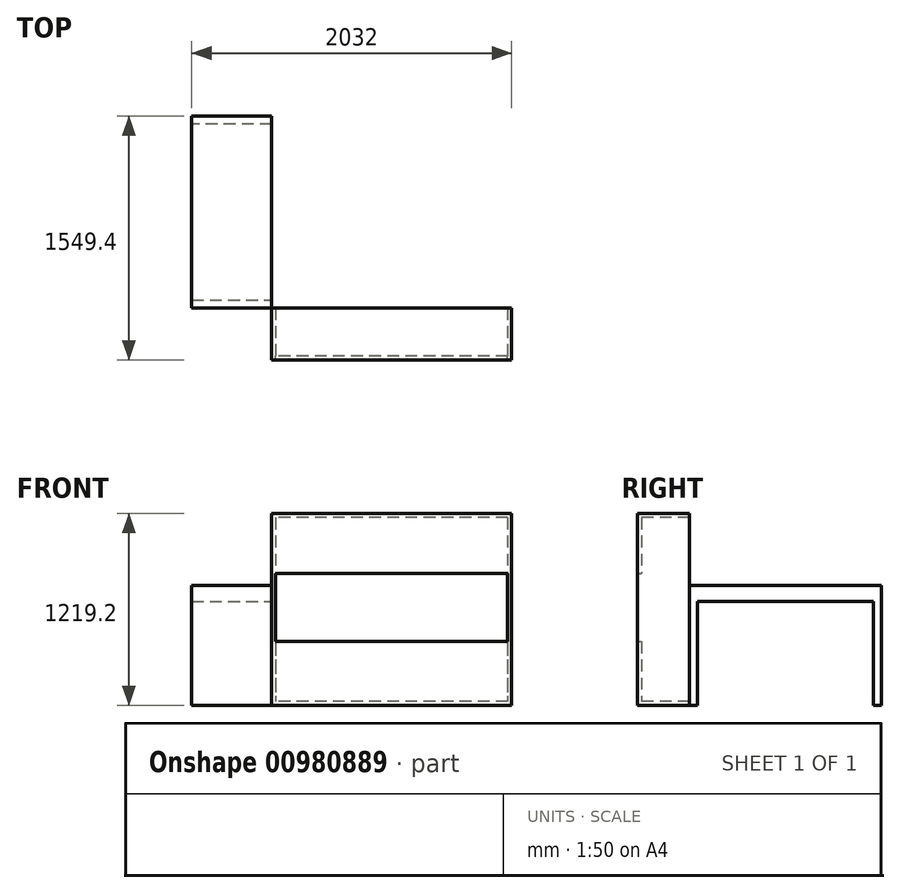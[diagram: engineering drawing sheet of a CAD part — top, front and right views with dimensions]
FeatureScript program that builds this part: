
annotation { "Feature Type Name" : "Feature", "Feature Type Description" : "" }
export const myFeature = defineFeature(function(context is Context, id is Id, definition is map)
    precondition{}
    {
        {
            var Q0;
            Q0=qCreatedBy(makeId("Front.planeOp"),FACE);
            var sketch = newSketch(context, id + "F0", { "sketchPlane" : qUnion([Q0])});
            skLineSegment(sketch, "E0.bottom", {"start": v(762, 609.6) * mm, "end": v(-762, 609.6) * mm});
            skLineSegment(sketch, "E0.top", {"start": v(762, -609.6) * mm, "end": v(-762, -609.6) * mm});
            skLineSegment(sketch, "E0.left", {"start": v(762, 609.6) * mm, "end": v(762, -609.6) * mm});
            skLineSegment(sketch, "E0.right", {"start": v(-762, 609.6) * mm, "end": v(-762, -609.6) * mm});
            skPoint(sketch, "E0.middle", {"position": v(0, 0) * mm});
            skLineSegment(sketch, "E1.0", {"start": v(736.6, 584.2) * mm, "end": v(736.6, -584.2) * mm});
            skLineSegment(sketch, "E1.1", {"start": v(736.6, 584.2) * mm, "end": v(-736.6, 584.2) * mm});
            skLineSegment(sketch, "E1.2", {"start": v(-736.6, 584.2) * mm, "end": v(-736.6, -584.2) * mm});
            skLineSegment(sketch, "E1.3", {"start": v(736.6, -584.2) * mm, "end": v(-736.6, -584.2) * mm});
            skLineSegment(sketch, "E2.0.1.0", {"start": v(736.6, -177.8) * mm, "end": v(-736.6, -177.8) * mm});
            skLineSegment(sketch, "E2.0.1.1", {"start": v(762, -203.2) * mm, "end": v(-762, -203.2) * mm});
            skLineSegment(sketch, "E2.0.2.0", {"start": v(736.6, 228.6) * mm, "end": v(-736.6, 228.6) * mm});
            skLineSegment(sketch, "E2.0.2.1", {"start": v(762, 203.2) * mm, "end": v(-762, 203.2) * mm});
            skLineSegment(sketch, "E2.1.1.0", {"start": v(736.6, -177.8) * mm, "end": v(-736.6, -177.8) * mm});
            skLineSegment(sketch, "E2.1.1.1", {"start": v(762, -203.2) * mm, "end": v(-762, -203.2) * mm});
            skLineSegment(sketch, "E2.1.2.0", {"start": v(736.6, 228.6) * mm, "end": v(-736.6, 228.6) * mm});
            skLineSegment(sketch, "E2.1.2.1", {"start": v(762, 203.2) * mm, "end": v(-762, 203.2) * mm});
            skLineSegment(sketch, "E2.2.1.0", {"start": v(736.6, -177.8) * mm, "end": v(-736.6, -177.8) * mm});
            skLineSegment(sketch, "E2.2.1.1", {"start": v(762, -203.2) * mm, "end": v(-762, -203.2) * mm});
            skLineSegment(sketch, "E2.2.2.0", {"start": v(736.6, 228.6) * mm, "end": v(-736.6, 228.6) * mm});
            skLineSegment(sketch, "E2.2.2.1", {"start": v(762, 203.2) * mm, "end": v(-762, 203.2) * mm});
            skLineSegment(sketch, "E2.direction1", {"start": v(-736.6, -584.2) * mm, "end": v(-736.6, -584.2) * mm});
            skLineSegment(sketch, "E2.direction2", {"start": v(-736.6, -584.2) * mm, "end": v(-736.6, -177.8) * mm, "construction": true});
            skSolve(sketch);
        }
        {
            var Q0;
            {var subQ0=sQuery(id+"F0.wireOp",EDGE,"E2.2.2.0");Q0=makeQuery(id+"F0.imprint","IMPRINT",FACE,{"disambiguationData":[TD([[makeQuery(id+"F0.imprint","IMPRINT",EDGE,{"derivedFrom":subQ0}),1.0]])]});}
            var Q1;
            {var subQ0=sQuery(id+"F0.wireOp",EDGE,"E2.2.1.1");var subQ1=sQuery(id+"F0.wireOp",EDGE,"E0.left");var subQ2=makeQuery(id+"F0.imprint","INTERSECT",VERTEX,{"derivedFrom":[subQ1,subQ0]});Q1=makeQuery(id+"F0.imprint","IMPRINT",FACE,{"disambiguationData":[TD([[makeQuery(id+"F0.imprint","IMPRINT",EDGE,{"disambiguationData":[TD([[subQ2,1.0]])],"derivedFrom":subQ1}),-1.0]])]});}
            var Q2;
            {var subQ0=sQuery(id+"F0.wireOp",EDGE,"E2.2.1.1");var subQ1=sQuery(id+"F0.wireOp",EDGE,"E0.right");var subQ2=makeQuery(id+"F0.imprint","INTERSECT",VERTEX,{"derivedFrom":[subQ1,subQ0]});Q2=makeQuery(id+"F0.imprint","IMPRINT",FACE,{"disambiguationData":[TD([[makeQuery(id+"F0.imprint","IMPRINT",EDGE,{"disambiguationData":[TD([[subQ2,1.0]])],"derivedFrom":subQ1}),1.0]])]});}
            var Q3;
            {var subQ0=sQuery(id+"F0.wireOp",EDGE,"E1.3");Q3=makeQuery(id+"F0.imprint","IMPRINT",FACE,{"disambiguationData":[TD([[makeQuery(id+"F0.imprint","IMPRINT",EDGE,{"derivedFrom":subQ0}),1.0]])]});}
            var Q4;
            {var subQ5=sQuery(id+"F0.wireOp",EDGE,"E0.bottom");Q4=makeQuery(id+"F0.imprint","IMPRINT",FACE,{"disambiguationData":[TD([[makeQuery(id+"F0.imprint","IMPRINT",EDGE,{"derivedFrom":subQ5}),1.0]])]});}
            var Q5;
            {var subQ0=sQuery(id+"F0.wireOp",EDGE,"E1.1");Q5=makeQuery(id+"F0.imprint","IMPRINT",FACE,{"disambiguationData":[TD([[makeQuery(id+"F0.imprint","IMPRINT",EDGE,{"derivedFrom":subQ0}),1.0]])]});}
            var Q6;
            {var subQ0=sQuery(id+"F0.wireOp",EDGE,"E2.2.1.0");Q6=makeQuery(id+"F0.imprint","IMPRINT",FACE,{"disambiguationData":[TD([[makeQuery(id+"F0.imprint","IMPRINT",EDGE,{"derivedFrom":subQ0}),-1.0]])]});}
            var Q7;
            {var subQ0=sQuery(id+"F0.wireOp",EDGE,"E1.3");Q7=makeQuery(id+"F0.imprint","IMPRINT",FACE,{"disambiguationData":[TD([[makeQuery(id+"F0.imprint","IMPRINT",EDGE,{"derivedFrom":subQ0}),-1.0]])]});}
            var Q8;
            {var subQ0=sQuery(id+"F0.wireOp",EDGE,"E2.2.1.0");Q8=makeQuery(id+"F0.imprint","IMPRINT",FACE,{"disambiguationData":[TD([[makeQuery(id+"F0.imprint","IMPRINT",EDGE,{"derivedFrom":subQ0}),1.0]])]});}
            extrude(context, id + "F1", {"entities" : qUnion([Q0, Q1, Q2, Q3, Q4, Q5, Q6, Q7, Q8]), "depth" : 25.4 * mm, "offsetDistance" : 25.4 * mm});
        }
        {
            var Q0;
            {var subQ0=sQuery(id+"F0.wireOp",EDGE,"E2.2.2.0");Q0=makeQuery(id+"F0.imprint","IMPRINT",FACE,{"disambiguationData":[TD([[makeQuery(id+"F0.imprint","IMPRINT",EDGE,{"derivedFrom":subQ0}),1.0]])]});}
            var Q1;
            {var subQ5=sQuery(id+"F0.wireOp",EDGE,"E0.bottom");Q1=makeQuery(id+"F0.imprint","IMPRINT",FACE,{"disambiguationData":[TD([[makeQuery(id+"F0.imprint","IMPRINT",EDGE,{"derivedFrom":subQ5}),1.0]])]});}
            var Q2;
            {var subQ0=sQuery(id+"F0.wireOp",EDGE,"E2.2.1.1");var subQ1=sQuery(id+"F0.wireOp",EDGE,"E0.right");var subQ2=makeQuery(id+"F0.imprint","INTERSECT",VERTEX,{"derivedFrom":[subQ1,subQ0]});Q2=makeQuery(id+"F0.imprint","IMPRINT",FACE,{"disambiguationData":[TD([[makeQuery(id+"F0.imprint","IMPRINT",EDGE,{"disambiguationData":[TD([[subQ2,1.0]])],"derivedFrom":subQ1}),1.0]])]});}
            var Q3;
            {var subQ0=sQuery(id+"F0.wireOp",EDGE,"E2.2.1.1");var subQ1=sQuery(id+"F0.wireOp",EDGE,"E0.left");var subQ2=makeQuery(id+"F0.imprint","INTERSECT",VERTEX,{"derivedFrom":[subQ1,subQ0]});Q3=makeQuery(id+"F0.imprint","IMPRINT",FACE,{"disambiguationData":[TD([[makeQuery(id+"F0.imprint","IMPRINT",EDGE,{"disambiguationData":[TD([[subQ2,1.0]])],"derivedFrom":subQ1}),-1.0]])]});}
            var Q4;
            {var subQ0=sQuery(id+"F0.wireOp",EDGE,"E2.2.1.0");Q4=makeQuery(id+"F0.imprint","IMPRINT",FACE,{"disambiguationData":[TD([[makeQuery(id+"F0.imprint","IMPRINT",EDGE,{"derivedFrom":subQ0}),1.0]])]});}
            var Q5;
            {var subQ0=sQuery(id+"F0.wireOp",EDGE,"E1.3");Q5=makeQuery(id+"F0.imprint","IMPRINT",FACE,{"disambiguationData":[TD([[makeQuery(id+"F0.imprint","IMPRINT",EDGE,{"derivedFrom":subQ0}),1.0]])]});}
            extrude(context, id + "F2", {"entities" : qUnion([Q0, Q1, Q2, Q3, Q4, Q5]), "operationType" : NewBodyOperationType.ADD, "oppositeDirection" : true, "depth" : 304.8 * mm, "offsetDistance" : 25.4 * mm});
        }
        {
            var Q0;
            {var subQ0=sQuery(id+"F0.wireOp",EDGE,"E0.bottom");Q0=makeQuery(id+"F2.boolean.opBoolean","MERGE",FACE,{"derivedFrom":[makeQuery(id+"F1.opExtrude","SWEPT_FACE",FACE,{"disambiguationData":[OSD([subQ0])]}),makeQuery(id+"F2.opExtrude","SWEPT_FACE",FACE,{"disambiguationData":[OSD([subQ0])]})]});}
            cPlane(context, id + "F3", {"entities" : qUnion([Q0]), "cplaneType" : CPlaneType.OFFSET, "offset" : 457.2 * mm, "oppositeDirection" : true, "width" : 152.4 * mm, "height" : 152.4 * mm});
        }
        {
            var Q0;
            Q0=qCreatedBy(id+"F3.planeOp",FACE);
            var sketch = newSketch(context, id + "F4", { "sketchPlane" : qUnion([Q0])});
            skLineSegment(sketch, "E3.bottom", {"start": v(-1270, 304.8) * mm, "end": v(-762, 304.8) * mm});
            skLineSegment(sketch, "E3.top", {"start": v(-1270, 1524) * mm, "end": v(-762, 1524) * mm});
            skLineSegment(sketch, "E3.left", {"start": v(-1270, 304.8) * mm, "end": v(-1270, 1524) * mm});
            skLineSegment(sketch, "E3.right", {"start": v(-762, 304.8) * mm, "end": v(-762, 1524) * mm});
            skSolve(sketch);
        }
        {
            var Q0;
            Q0=makeQuery(id+"F4.imprint","IMPRINT",FACE,{"disambiguationData":[TD([[makeQuery(id+"F4.imprint","IMPRINT",EDGE,{"derivedFrom":sQuery(id+"F4.wireOp",EDGE,"E3.bottom")}),1.0]])]});
            extrude(context, id + "F5", {"entities" : qUnion([Q0]), "oppositeDirection" : true, "depth" : 101.6 * mm, "offsetDistance" : 25.4 * mm});
        }
        {
            var Q0;
            Q0=makeQuery(id+"F5.opExtrude","CAP_FACE",FACE,{"disambiguationData":[OSD([sQuery(id+"F4.wireOp",EDGE,"E3.bottom"),sQuery(id+"F4.wireOp",EDGE,"E3.top"),sQuery(id+"F4.wireOp",EDGE,"E3.left"),sQuery(id+"F4.wireOp",EDGE,"E3.right")])],"isStart":false});
            var sketch = newSketch(context, id + "F6", { "sketchPlane" : qUnion([Q0])});
            skLineSegment(sketch, "E4.bottom", {"start": v(-762, -1524) * mm, "end": v(-1270, -1524) * mm});
            skLineSegment(sketch, "E4.top", {"start": v(-762, -1473.2) * mm, "end": v(-1270, -1473.2) * mm});
            skLineSegment(sketch, "E4.left", {"start": v(-762, -1524) * mm, "end": v(-762, -1473.2) * mm});
            skLineSegment(sketch, "E4.right", {"start": v(-1270, -1524) * mm, "end": v(-1270, -1473.2) * mm});
            skLineSegment(sketch, "E5.bottom", {"start": v(-1270, -304.8) * mm, "end": v(-762, -304.8) * mm});
            skLineSegment(sketch, "E5.top", {"start": v(-1270, -355.6) * mm, "end": v(-762, -355.6) * mm});
            skLineSegment(sketch, "E5.left", {"start": v(-1270, -304.8) * mm, "end": v(-1270, -355.6) * mm});
            skLineSegment(sketch, "E5.right", {"start": v(-762, -304.8) * mm, "end": v(-762, -355.6) * mm});
            skSolve(sketch);
        }
        {
            var Q0;
            Q0=makeQuery(id+"F6.imprint","IMPRINT",FACE,{"disambiguationData":[TD([[makeQuery(id+"F6.imprint","IMPRINT",EDGE,{"derivedFrom":sQuery(id+"F6.wireOp",EDGE,"E4.bottom")}),1.0]])]});
            var Q1;
            Q1=makeQuery(id+"F6.imprint","IMPRINT",FACE,{"disambiguationData":[TD([[makeQuery(id+"F6.imprint","IMPRINT",EDGE,{"derivedFrom":sQuery(id+"F6.wireOp",EDGE,"E5.top")}),1.0]])]});
            var Q2;
            {var subQ0=sQuery(id+"F0.wireOp",EDGE,"E0.top");Q2=makeQuery(id+"F2.boolean.opBoolean","MERGE",FACE,{"derivedFrom":[makeQuery(id+"F1.opExtrude","SWEPT_FACE",FACE,{"disambiguationData":[OSD([subQ0])]}),makeQuery(id+"F2.opExtrude","SWEPT_FACE",FACE,{"disambiguationData":[OSD([subQ0])]})]});}
            extrude(context, id + "F7", {"entities" : qUnion([Q0, Q1]), "operationType" : NewBodyOperationType.ADD, "endBound" : BoundingType.UP_TO_SURFACE, "depth" : 25.4 * mm, "endBoundEntityFace" : qUnion([Q2]), "offsetDistance" : 25.4 * mm});
        }
    });
